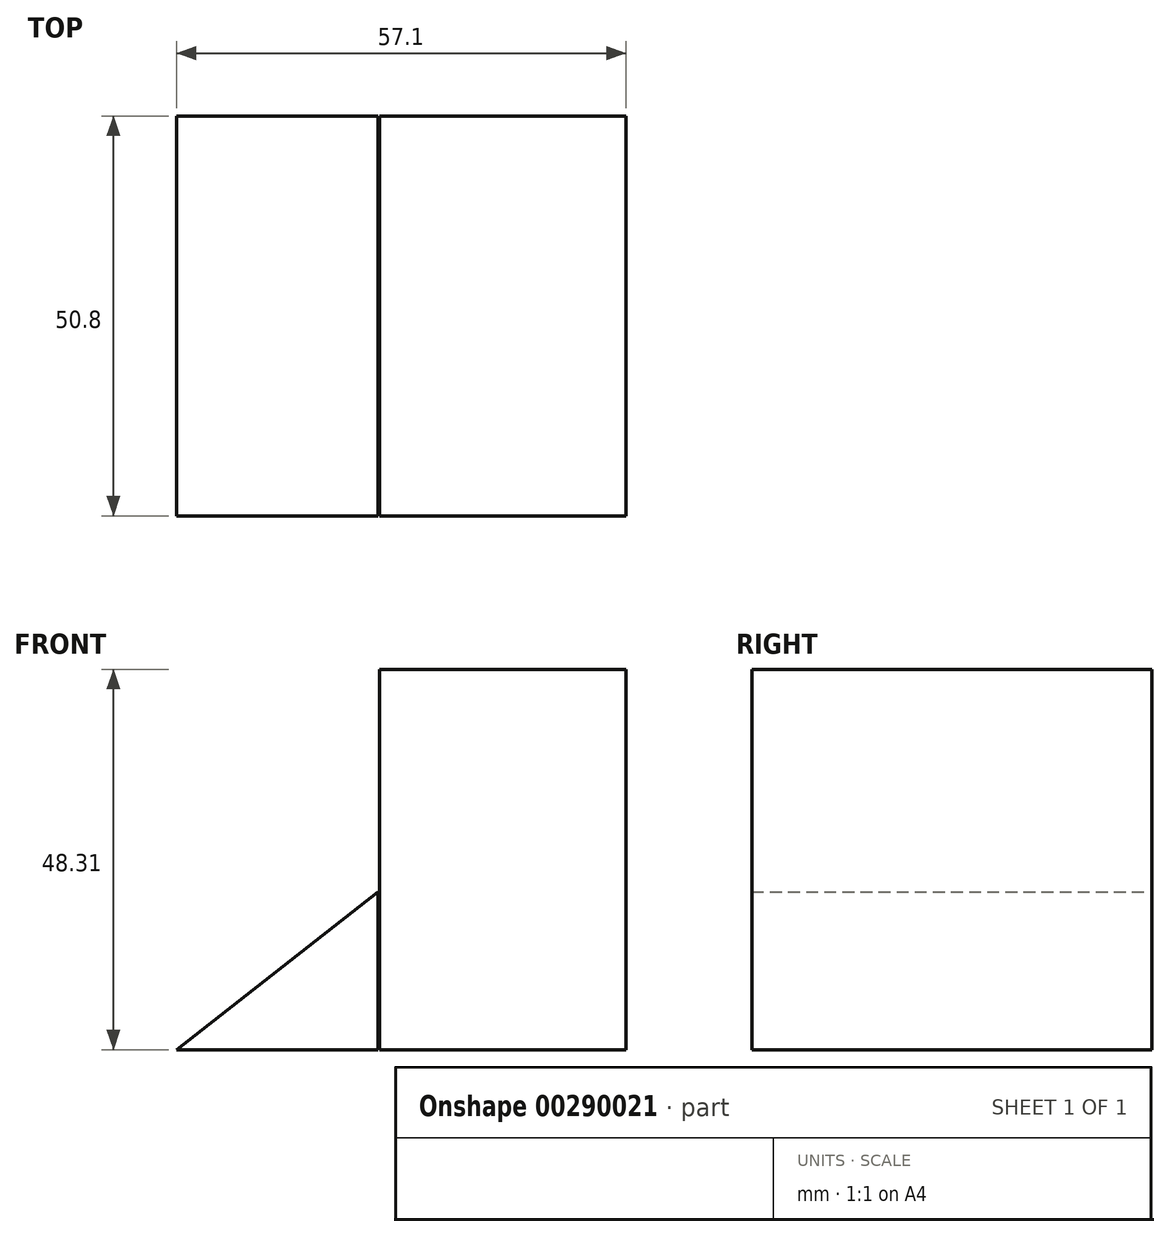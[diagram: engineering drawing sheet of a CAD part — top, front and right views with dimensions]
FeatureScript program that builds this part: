
annotation { "Feature Type Name" : "Feature", "Feature Type Description" : "" }
export const myFeature = defineFeature(function(context is Context, id is Id, definition is map)
    precondition{}
    {
        {
            var Q0;
            Q0=qCreatedBy(makeId("Front.planeOp"),FACE);
            var sketch = newSketch(context, id + "F0", { "sketchPlane" : qUnion([Q0])});
            skLineSegment(sketch, "E0.bottom", {"start": v(0, 0) * mm, "end": v(-31.32, 0) * mm});
            skLineSegment(sketch, "E0.top", {"start": v(0, 48.31) * mm, "end": v(-31.32, 48.31) * mm});
            skLineSegment(sketch, "E0.left", {"start": v(0, 0) * mm, "end": v(0, 48.31) * mm});
            skLineSegment(sketch, "E0.right", {"start": v(-31.32, 0) * mm, "end": v(-31.32, 48.31) * mm});
            skSolve(sketch);
        }
        {
            var Q0;
            Q0=makeQuery(id+"F0.imprint","IMPRINT",FACE,{"disambiguationData":[TD([[makeQuery(id+"F0.imprint","IMPRINT",EDGE,{"derivedFrom":sQuery(id+"F0.wireOp",EDGE,"E0.bottom")}),-1.0]])]});
            extrude(context, id + "F1", {"entities" : qUnion([Q0]), "depth" : 50.8 * mm});
        }
        {
            var Q0;
            Q0=qCreatedBy(makeId("Front.planeOp"),FACE);
            var sketch = newSketch(context, id + "F2", { "sketchPlane" : qUnion([Q0])});
            skLineSegment(sketch, "E1", {"start": v(-57.1, 0) * mm, "end": v(-31.5, 20.05) * mm});
            skLineSegment(sketch, "E2", {"start": v(-31.5, 20.05) * mm, "end": v(-31.5, 0) * mm});
            skLineSegment(sketch, "E3", {"start": v(-31.5, 0) * mm, "end": v(-57.1, 0) * mm});
            skSolve(sketch);
        }
        {
            var Q0;
            Q0=makeQuery(id+"F2.imprint","IMPRINT",FACE,{"disambiguationData":[TD([[makeQuery(id+"F2.imprint","IMPRINT",EDGE,{"derivedFrom":sQuery(id+"F2.wireOp",EDGE,"E1")}),-1.0]])]});
            extrude(context, id + "F3", {"entities" : qUnion([Q0]), "depth" : 50.8 * mm});
        }
    });
